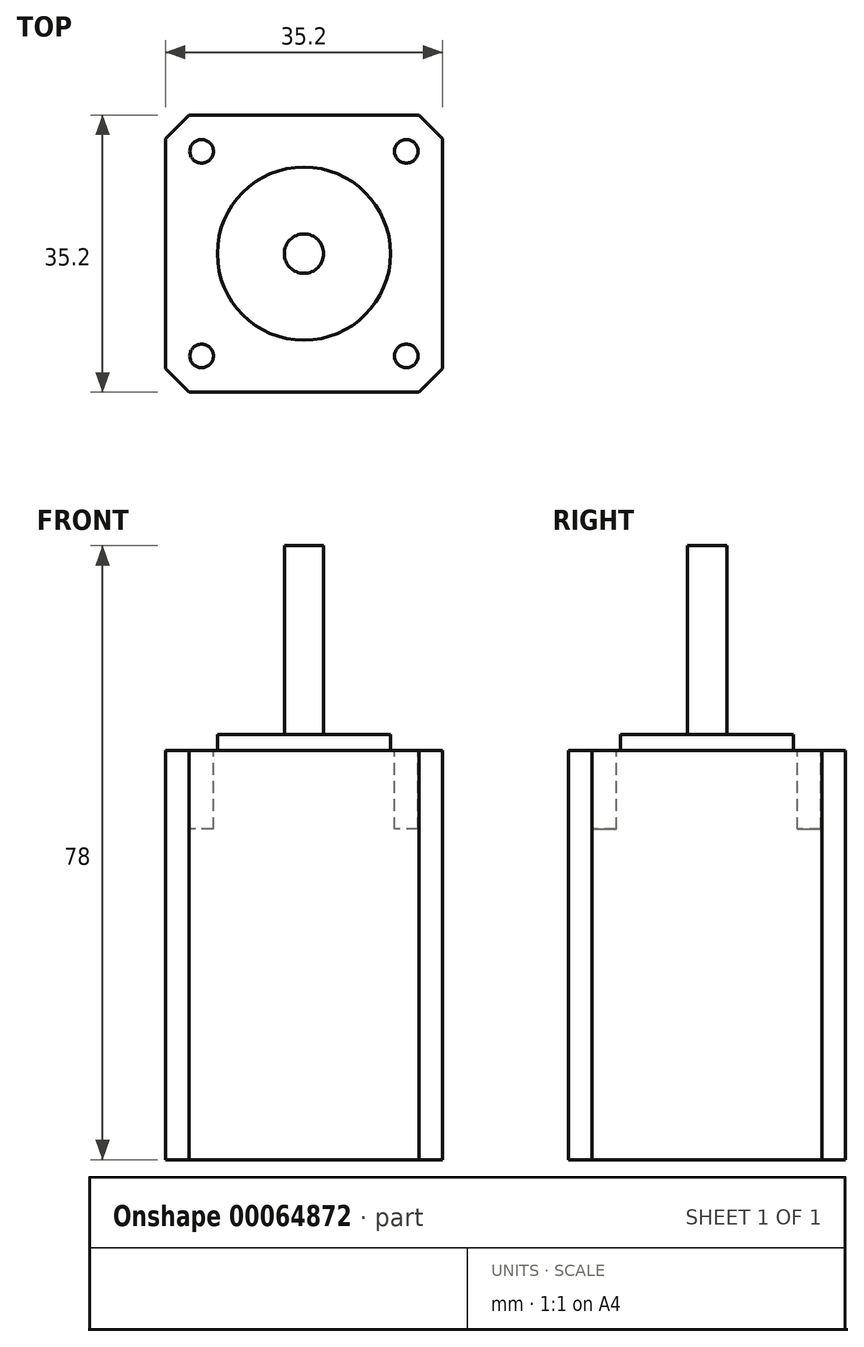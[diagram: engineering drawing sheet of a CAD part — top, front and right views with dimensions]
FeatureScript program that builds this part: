
annotation { "Feature Type Name" : "Feature", "Feature Type Description" : "" }
export const myFeature = defineFeature(function(context is Context, id is Id, definition is map)
    precondition{}
    {
        {
            var Q0;
            Q0=qCreatedBy(makeId("Top.planeOp"),FACE);
            var sketch = newSketch(context, id + "F0", { "sketchPlane" : qUnion([Q0])});
            skLineSegment(sketch, "E0.bottom", {"start": v(0, 0) * mm, "end": v(35.2, 0) * mm});
            skLineSegment(sketch, "E0.top", {"start": v(0, 35.2) * mm, "end": v(35.2, 35.2) * mm});
            skLineSegment(sketch, "E0.left", {"start": v(0, 0) * mm, "end": v(0, 35.2) * mm});
            skLineSegment(sketch, "E0.right", {"start": v(35.2, 0) * mm, "end": v(35.2, 35.2) * mm});
            skSolve(sketch);
        }
        {
            var Q0;
            Q0=qSketchRegion(id+"F0",true);
            extrude(context, id + "F1", {"entities" : qUnion([Q0]), "depth" : 52 * mm});
        }
        {
            var Q0;
            Q0=makeQuery(id+"F1.opExtrude","SWEPT_EDGE",EDGE,{"disambiguationData":[OSD([sQuery(id+"F0.wireOp",EDGE,"E0.bottom"),sQuery(id+"F0.wireOp",EDGE,"E0.left")])]});
            var Q1;
            Q1=makeQuery(id+"F1.opExtrude","SWEPT_EDGE",EDGE,{"disambiguationData":[OSD([sQuery(id+"F0.wireOp",EDGE,"E0.top"),sQuery(id+"F0.wireOp",EDGE,"E0.left")])]});
            var Q2;
            Q2=makeQuery(id+"F1.opExtrude","SWEPT_EDGE",EDGE,{"disambiguationData":[OSD([sQuery(id+"F0.wireOp",EDGE,"E0.bottom"),sQuery(id+"F0.wireOp",EDGE,"E0.right")])]});
            var Q3;
            Q3=makeQuery(id+"F1.opExtrude","SWEPT_EDGE",EDGE,{"disambiguationData":[OSD([sQuery(id+"F0.wireOp",EDGE,"E0.top"),sQuery(id+"F0.wireOp",EDGE,"E0.right")])]});
            chamfer(context, id + "F2", {"entities" : qUnion([Q0, Q1, Q2, Q3]), "width" : 3 * mm, "tangentPropagation" : true});
        }
        {
            var Q0;
            Q0=makeQuery(id+"F1.opExtrude","CAP_FACE",FACE,{"disambiguationData":[OSD([sQuery(id+"F0.wireOp",EDGE,"E0.bottom"),sQuery(id+"F0.wireOp",EDGE,"E0.top"),sQuery(id+"F0.wireOp",EDGE,"E0.left"),sQuery(id+"F0.wireOp",EDGE,"E0.right")])],"isStart":false});
            var sketch = newSketch(context, id + "F3", { "sketchPlane" : qUnion([Q0])});
            skCircle(sketch, "E1", {"center": v(17.6, 17.6) * mm, "radius": 11 * mm});
            skLineSegment(sketch, "E2", {"start": v(17.6, 35.2) * mm, "end": v(17.6, 0) * mm, "construction": true});
            skSolve(sketch);
        }
        {
            var Q0;
            Q0=qSketchRegion(id+"F3",true);
            extrude(context, id + "F4", {"entities" : qUnion([Q0]), "operationType" : NewBodyOperationType.ADD, "depth" : 2 * mm});
        }
        {
            var Q0;
            Q0=makeQuery(id+"F4.opExtrude","CAP_FACE",FACE,{"disambiguationData":[OSD([sQuery(id+"F3.wireOp",EDGE,"E1")])],"isStart":false});
            var sketch = newSketch(context, id + "F5", { "sketchPlane" : qUnion([Q0])});
            skCircle(sketch, "E3", {"center": v(17.6, 17.6) * mm, "radius": 2.5 * mm});
            skSolve(sketch);
        }
        {
            var Q0;
            Q0=qSketchRegion(id+"F5",true);
            var Q1;
            Q1=qSketchRegion(id+"F7",true);
            extrude(context, id + "F6", {"entities" : qUnion([Q0, Q1]), "operationType" : NewBodyOperationType.ADD, "depth" : 24 * mm});
        }
        {
            var Q0;
            Q0=makeQuery(id+"F1.opExtrude","CAP_FACE",FACE,{"disambiguationData":[OSD([sQuery(id+"F0.wireOp",EDGE,"E0.bottom"),sQuery(id+"F0.wireOp",EDGE,"E0.top"),sQuery(id+"F0.wireOp",EDGE,"E0.left"),sQuery(id+"F0.wireOp",EDGE,"E0.right")])],"isStart":false});
            var sketch = newSketch(context, id + "F7", { "sketchPlane" : qUnion([Q0])});
            skCircle(sketch, "E4", {"center": v(4.6, 30.6) * mm, "radius": 1.5 * mm});
            skCircle(sketch, "E5", {"center": v(4.6, 4.6) * mm, "radius": 1.5 * mm});
            skCircle(sketch, "E6", {"center": v(30.6, 30.6) * mm, "radius": 1.5 * mm});
            skCircle(sketch, "E7", {"center": v(30.6, 4.6) * mm, "radius": 1.5 * mm});
            skLineSegment(sketch, "E8", {"start": v(0, 17.6) * mm, "end": v(35.2, 17.6) * mm, "construction": true});
            skLineSegment(sketch, "E9", {"start": v(17.6, 17.6) * mm, "end": v(17.6, 35.2) * mm, "construction": true});
            skSolve(sketch);
        }
        {
            var Q0;
            Q0=qSketchRegion(id+"F7",true);
            extrude(context, id + "F8", {"entities" : qUnion([Q0]), "operationType" : NewBodyOperationType.REMOVE, "oppositeDirection" : true, "depth" : 10 * mm});
        }
    });
